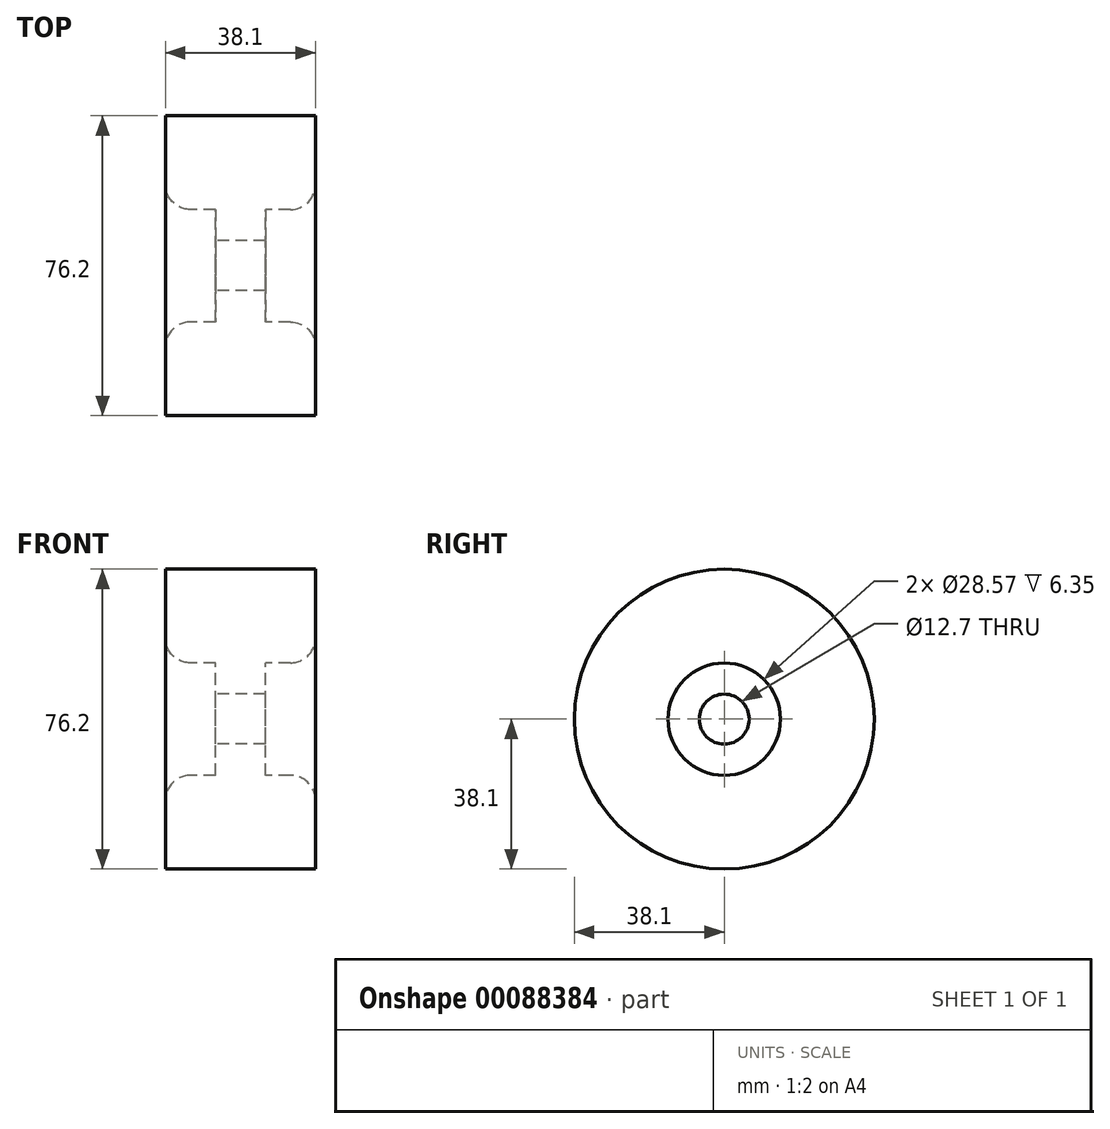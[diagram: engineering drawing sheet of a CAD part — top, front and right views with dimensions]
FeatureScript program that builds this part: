
annotation { "Feature Type Name" : "Feature", "Feature Type Description" : "" }
export const myFeature = defineFeature(function(context is Context, id is Id, definition is map)
    precondition{}
    {
        {
            var Q0;
            Q0=qCreatedBy(makeId("Right.planeOp"),FACE);
            var sketch = newSketch(context, id + "F0", { "sketchPlane" : qUnion([Q0])});
            skCircle(sketch, "E0", {"center": v(0, 0) * mm, "radius": 38.1 * mm});
            skCircle(sketch, "E1", {"center": v(0, 0) * mm, "radius": 14.29 * mm});
            skCircle(sketch, "E2", {"center": v(0, 0) * mm, "radius": 6.35 * mm});
            skSolve(sketch);
        }
        {
            var Q0;
            Q0=makeQuery(id+"F0.imprint","IMPRINT",FACE,{"disambiguationData":[TD([[makeQuery(id+"F0.imprint","IMPRINT",EDGE,{"derivedFrom":sQuery(id+"F0.wireOp",EDGE,"E0")}),1.0]])]});
            extrude(context, id + "F1", {"entities" : qUnion([Q0]), "endBound" : BoundingType.SYMMETRIC, "depth" : 38.1 * mm});
        }
        {
            var Q0;
            Q0=makeQuery(id+"F0.imprint","IMPRINT",FACE,{"disambiguationData":[TD([[makeQuery(id+"F0.imprint","IMPRINT",EDGE,{"derivedFrom":sQuery(id+"F0.wireOp",EDGE,"E1")}),1.0]])]});
            extrude(context, id + "F2", {"entities" : qUnion([Q0]), "operationType" : NewBodyOperationType.ADD, "endBound" : BoundingType.SYMMETRIC, "depth" : 12.7 * mm});
        }
        {
            var Q0;
            Q0=makeQuery(id+"F1.opExtrude","CAP_EDGE",EDGE,{"disambiguationData":[OSD([sQuery(id+"F0.wireOp",EDGE,"E1")])],"isStart":true});
            var Q1;
            Q1=makeQuery(id+"F1.opExtrude","CAP_EDGE",EDGE,{"disambiguationData":[OSD([sQuery(id+"F0.wireOp",EDGE,"E1")])],"isStart":false});
            fillet(context, id + "F3", {"entities" : qUnion([Q0, Q1]), "radius" : 6.35 * mm, "tangentPropagation" : true, "allowEdgeOverflow" : false});
        }
    });
